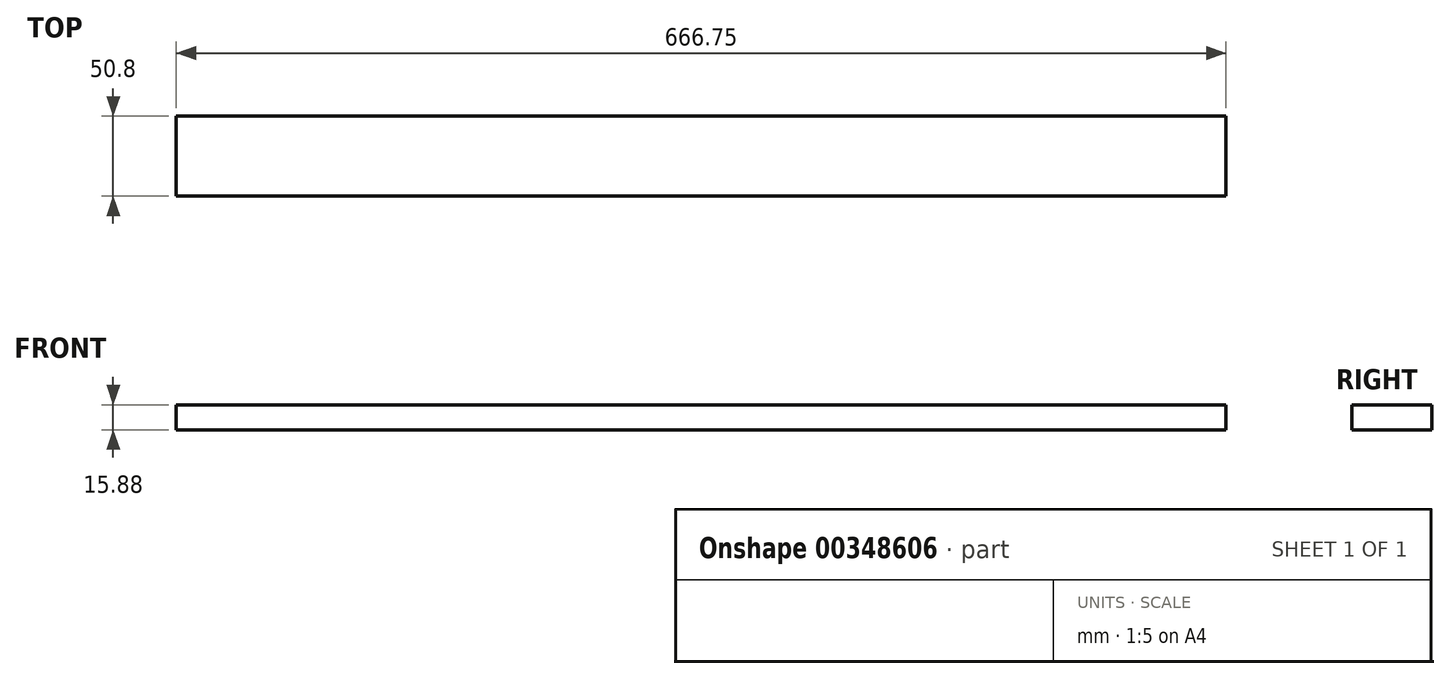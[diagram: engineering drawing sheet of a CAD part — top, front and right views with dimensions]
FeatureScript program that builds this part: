
annotation { "Feature Type Name" : "Feature", "Feature Type Description" : "" }
export const myFeature = defineFeature(function(context is Context, id is Id, definition is map)
    precondition{}
    {
        {
            var Q0;
            Q0=qCreatedBy(makeId("Top.planeOp"),FACE);
            var sketch = newSketch(context, id + "F0", { "sketchPlane" : qUnion([Q0])});
            skLineSegment(sketch, "E0.bottom", {"start": v(-138.3, 30.97) * mm, "end": v(528.44, 30.97) * mm});
            skLineSegment(sketch, "E0.top", {"start": v(-138.3, -19.83) * mm, "end": v(528.44, -19.83) * mm});
            skLineSegment(sketch, "E0.left", {"start": v(-138.3, 30.97) * mm, "end": v(-138.3, -19.83) * mm});
            skLineSegment(sketch, "E0.right", {"start": v(528.44, 30.97) * mm, "end": v(528.44, -19.83) * mm});
            skSolve(sketch);
        }
        {
            var Q0;
            Q0 = qSketchRegion(id + "F0", true);
            extrude(context, id + "F1", {"entities" : qUnion([Q0]), "depth" : 15.88 * mm});
        }
    });
